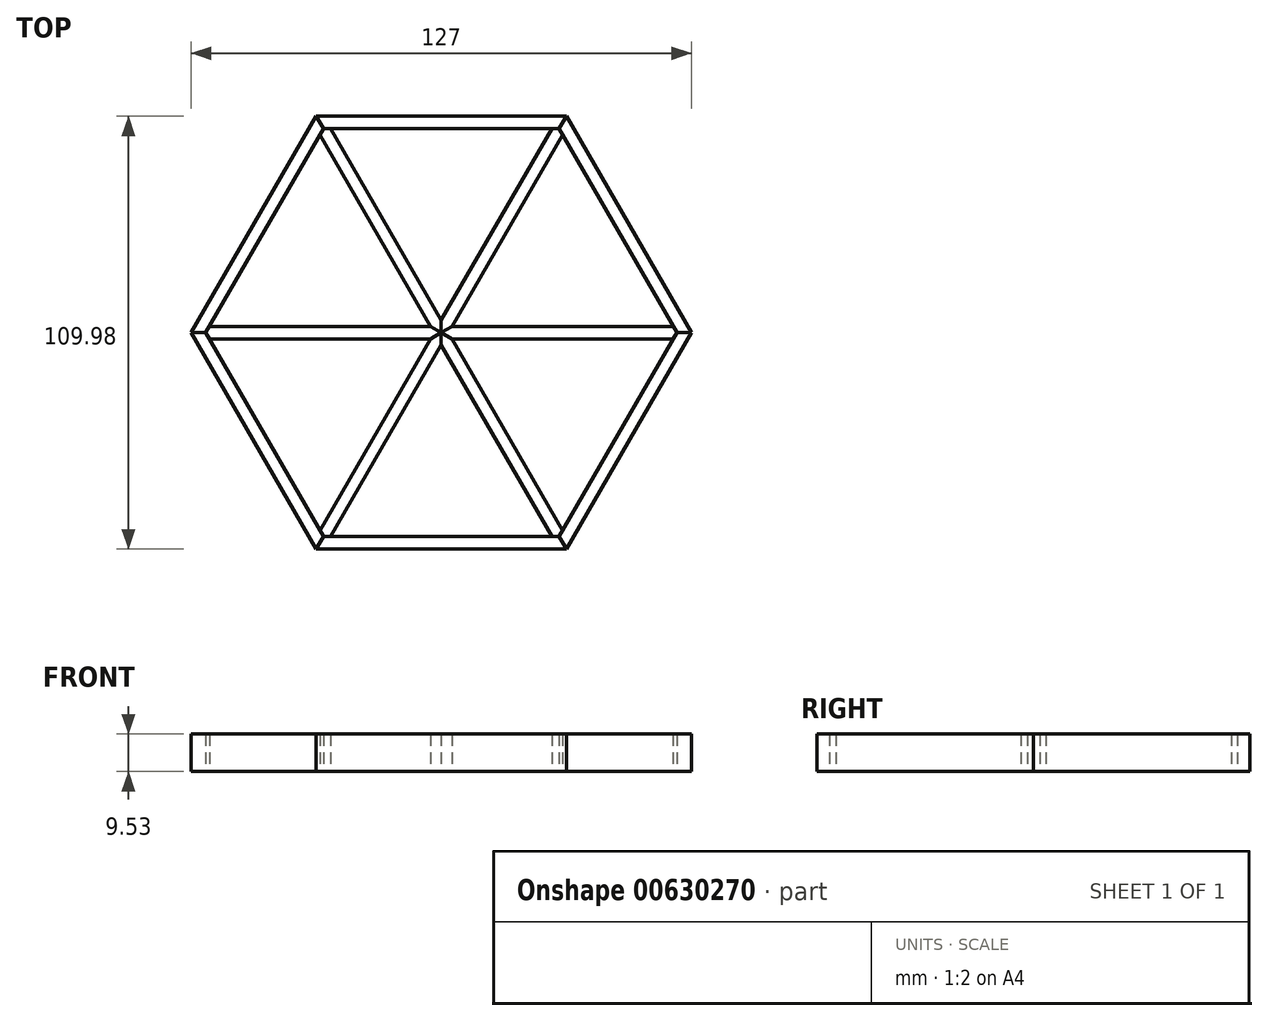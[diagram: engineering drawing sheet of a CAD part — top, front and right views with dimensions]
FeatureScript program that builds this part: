
annotation { "Feature Type Name" : "Feature", "Feature Type Description" : "" }
export const myFeature = defineFeature(function(context is Context, id is Id, definition is map)
    precondition{}
    {
        {
            var Q0;
            Q0=qCreatedBy(makeId("Top.planeOp"),FACE);
            var sketch = newSketch(context, id + "F0", { "sketchPlane" : qUnion([Q0])});
            skCircle(sketch, "E0.cCircle", {"center": v(0, 0) * mm, "radius": 51.82 * mm, "construction": true});
            skLineSegment(sketch, "E0.0", {"start": v(29.92, 51.82) * mm, "end": v(59.83, 0) * mm});
            skLineSegment(sketch, "E0.1", {"start": v(59.83, 0) * mm, "end": v(29.92, -51.82) * mm});
            skLineSegment(sketch, "E0.2", {"start": v(29.92, -51.82) * mm, "end": v(-29.92, -51.82) * mm});
            skLineSegment(sketch, "E0.3", {"start": v(-29.92, -51.82) * mm, "end": v(-59.83, 0) * mm});
            skLineSegment(sketch, "E0.4", {"start": v(-59.83, 0) * mm, "end": v(-29.92, 51.82) * mm});
            skLineSegment(sketch, "E0.5", {"start": v(-29.92, 51.82) * mm, "end": v(29.92, 51.82) * mm});
            skPoint(sketch, "E0.0.midPoint", {"position": v(44.88, 25.9) * mm});
            skCircle(sketch, "E1.cCircle", {"center": v(0, 0) * mm, "radius": 55 * mm, "construction": true});
            skLineSegment(sketch, "E1.0", {"start": v(31.75, 55) * mm, "end": v(63.5, 0) * mm});
            skLineSegment(sketch, "E1.1", {"start": v(63.5, 0) * mm, "end": v(31.75, -55) * mm});
            skLineSegment(sketch, "E1.2", {"start": v(31.75, -55) * mm, "end": v(-31.75, -55) * mm});
            skLineSegment(sketch, "E1.3", {"start": v(-31.75, -55) * mm, "end": v(-63.5, 0) * mm});
            skLineSegment(sketch, "E1.4", {"start": v(-63.5, 0) * mm, "end": v(-31.75, 55) * mm});
            skLineSegment(sketch, "E1.5", {"start": v(-31.75, 55) * mm, "end": v(31.75, 55) * mm});
            skPoint(sketch, "E1.0.midPoint", {"position": v(47.62, 27.5) * mm});
            skLineSegment(sketch, "E2", {"start": v(-31.75, 55) * mm, "end": v(-29.92, 51.82) * mm});
            skLineSegment(sketch, "E3", {"start": v(31.75, 55) * mm, "end": v(29.92, 51.82) * mm});
            skLineSegment(sketch, "E4", {"start": v(63.5, 0) * mm, "end": v(59.83, 0) * mm});
            skLineSegment(sketch, "E5", {"start": v(31.75, -55) * mm, "end": v(29.92, -51.82) * mm});
            skLineSegment(sketch, "E6", {"start": v(-31.75, -55) * mm, "end": v(-29.92, -51.82) * mm});
            skLineSegment(sketch, "E7", {"start": v(-59.83, 0) * mm, "end": v(-63.5, 0) * mm});
            skSolve(sketch);
        }
        {
            var Q0;
            Q0=makeQuery(id+"F0.imprint","IMPRINT",FACE,{"disambiguationData":[TD([[makeQuery(id+"F0.imprint","IMPRINT",EDGE,{"derivedFrom":sQuery(id+"F0.wireOp",EDGE,"E0.4")}),1.0]])]});
            var Q1;
            Q1=makeQuery(id+"F0.imprint","IMPRINT",FACE,{"disambiguationData":[TD([[makeQuery(id+"F0.imprint","IMPRINT",EDGE,{"derivedFrom":sQuery(id+"F0.wireOp",EDGE,"E0.0")}),1.0]])]});
            var Q2;
            Q2=makeQuery(id+"F0.imprint","IMPRINT",FACE,{"disambiguationData":[TD([[makeQuery(id+"F0.imprint","IMPRINT",EDGE,{"derivedFrom":sQuery(id+"F0.wireOp",EDGE,"E0.2")}),1.0]])]});
            extrude(context, id + "F1", {"entities" : qUnion([Q0, Q1, Q2]), "depth" : 9.52 * mm, "offsetDistance" : 25.4 * mm});
        }
        {
            var Q0;
            Q0=makeQuery(id+"F0.imprint","IMPRINT",FACE,{"disambiguationData":[TD([[makeQuery(id+"F0.imprint","IMPRINT",EDGE,{"derivedFrom":sQuery(id+"F0.wireOp",EDGE,"E0.3")}),1.0]])]});
            var Q1;
            Q1=makeQuery(id+"F0.imprint","IMPRINT",FACE,{"disambiguationData":[TD([[makeQuery(id+"F0.imprint","IMPRINT",EDGE,{"derivedFrom":sQuery(id+"F0.wireOp",EDGE,"E0.5")}),1.0]])]});
            var Q2;
            Q2=makeQuery(id+"F0.imprint","IMPRINT",FACE,{"disambiguationData":[TD([[makeQuery(id+"F0.imprint","IMPRINT",EDGE,{"derivedFrom":sQuery(id+"F0.wireOp",EDGE,"E0.1")}),1.0]])]});
            extrude(context, id + "F2", {"entities" : qUnion([Q0, Q1, Q2]), "depth" : 9.52 * mm, "offsetDistance" : 25.4 * mm});
        }
        {
            var Q0;
            Q0=qCreatedBy(makeId("Top.planeOp"),FACE);
            var sketch = newSketch(context, id + "F3", { "sketchPlane" : qUnion([Q0])});
            skLineSegment(sketch, "E8", {"start": v(-30.83, 50.23) * mm, "end": v(-2.75, 1.59) * mm});
            skLineSegment(sketch, "E9", {"start": v(-2.75, 1.59) * mm, "end": v(0, 0) * mm});
            skLineSegment(sketch, "E10", {"start": v(0, 0) * mm, "end": v(0, 3.18) * mm});
            skLineSegment(sketch, "E11", {"start": v(0, 3.18) * mm, "end": v(-28.08, 51.82) * mm});
            skLineSegment(sketch, "E12", {"start": v(-28.08, 51.82) * mm, "end": v(-29.92, 51.82) * mm});
            skLineSegment(sketch, "E13", {"start": v(-29.92, 51.82) * mm, "end": v(-30.83, 50.23) * mm});
            skLineSegment(sketch, "E14", {"start": v(-2.75, 1.59) * mm, "end": v(-58.92, 1.59) * mm});
            skLineSegment(sketch, "E15", {"start": v(-58.92, 1.59) * mm, "end": v(-59.83, 0) * mm});
            skLineSegment(sketch, "E16", {"start": v(-59.83, 0) * mm, "end": v(-58.92, -1.59) * mm});
            skLineSegment(sketch, "E17", {"start": v(-58.92, -1.59) * mm, "end": v(-2.75, -1.59) * mm});
            skLineSegment(sketch, "E18", {"start": v(-2.75, -1.59) * mm, "end": v(0, 0) * mm});
            skLineSegment(sketch, "E19", {"start": v(-30.83, -50.23) * mm, "end": v(-29.92, -51.82) * mm});
            skLineSegment(sketch, "E20", {"start": v(-29.92, -51.82) * mm, "end": v(-28.08, -51.82) * mm});
            skLineSegment(sketch, "E21", {"start": v(0, -3.18) * mm, "end": v(0, 0) * mm});
            skLineSegment(sketch, "E22", {"start": v(-30.83, -50.23) * mm, "end": v(-2.75, -1.59) * mm});
            skLineSegment(sketch, "E23", {"start": v(-28.08, -51.82) * mm, "end": v(0, -3.18) * mm});
            skLineSegment(sketch, "E24", {"start": v(0, 0) * mm, "end": v(2.75, -1.59) * mm});
            skLineSegment(sketch, "E25", {"start": v(30.83, -50.23) * mm, "end": v(2.75, -1.59) * mm});
            skLineSegment(sketch, "E26", {"start": v(0, 0) * mm, "end": v(2.75, 1.59) * mm});
            skLineSegment(sketch, "E27", {"start": v(2.75, 1.59) * mm, "end": v(30.83, 50.23) * mm});
            skLineSegment(sketch, "E28", {"start": v(0, -3.18) * mm, "end": v(28.08, -51.82) * mm});
            skLineSegment(sketch, "E29", {"start": v(28.08, -51.82) * mm, "end": v(29.92, -51.82) * mm});
            skLineSegment(sketch, "E30", {"start": v(29.92, -51.82) * mm, "end": v(30.83, -50.23) * mm});
            skLineSegment(sketch, "E31", {"start": v(0, 3.18) * mm, "end": v(28.08, 51.82) * mm});
            skLineSegment(sketch, "E32", {"start": v(28.08, 51.82) * mm, "end": v(29.92, 51.82) * mm});
            skLineSegment(sketch, "E33", {"start": v(29.92, 51.82) * mm, "end": v(30.83, 50.23) * mm});
            skLineSegment(sketch, "E34", {"start": v(2.75, 1.59) * mm, "end": v(58.92, 1.59) * mm});
            skLineSegment(sketch, "E35", {"start": v(58.92, 1.59) * mm, "end": v(59.83, 0) * mm});
            skLineSegment(sketch, "E36", {"start": v(59.83, 0) * mm, "end": v(58.92, -1.59) * mm});
            skLineSegment(sketch, "E37", {"start": v(58.92, -1.59) * mm, "end": v(2.75, -1.59) * mm});
            skSolve(sketch);
        }
        {
            var Q0;
            Q0=makeQuery(id+"F3.imprint","IMPRINT",FACE,{"disambiguationData":[TD([[makeQuery(id+"F3.imprint","IMPRINT",EDGE,{"derivedFrom":sQuery(id+"F3.wireOp",EDGE,"E8")}),1.0]])]});
            var Q1;
            Q1=makeQuery(id+"F3.imprint","IMPRINT",FACE,{"disambiguationData":[TD([[makeQuery(id+"F3.imprint","IMPRINT",EDGE,{"derivedFrom":sQuery(id+"F3.wireOp",EDGE,"E21")}),-1.0]])]});
            extrude(context, id + "F4", {"entities" : qUnion([Q0, Q1]), "depth" : 9.52 * mm, "offsetDistance" : 25.4 * mm});
        }
        {
            var Q0;
            Q0=makeQuery(id+"F3.imprint","IMPRINT",FACE,{"disambiguationData":[TD([[makeQuery(id+"F3.imprint","IMPRINT",EDGE,{"derivedFrom":sQuery(id+"F3.wireOp",EDGE,"E9")}),-1.0]])]});
            var Q1;
            Q1=makeQuery(id+"F3.imprint","IMPRINT",FACE,{"disambiguationData":[TD([[makeQuery(id+"F3.imprint","IMPRINT",EDGE,{"derivedFrom":sQuery(id+"F3.wireOp",EDGE,"E24")}),1.0]])]});
            extrude(context, id + "F5", {"entities" : qUnion([Q0, Q1]), "depth" : 9.52 * mm, "offsetDistance" : 25.4 * mm});
        }
        {
            var Q0;
            Q0=makeQuery(id+"F3.imprint","IMPRINT",FACE,{"disambiguationData":[TD([[makeQuery(id+"F3.imprint","IMPRINT",EDGE,{"derivedFrom":sQuery(id+"F3.wireOp",EDGE,"E10")}),-1.0]])]});
            var Q1;
            Q1=makeQuery(id+"F3.imprint","IMPRINT",FACE,{"disambiguationData":[TD([[makeQuery(id+"F3.imprint","IMPRINT",EDGE,{"derivedFrom":sQuery(id+"F3.wireOp",EDGE,"E18")}),-1.0]])]});
            extrude(context, id + "F6", {"entities" : qUnion([Q0, Q1]), "depth" : 9.52 * mm, "offsetDistance" : 25.4 * mm});
        }
    });
